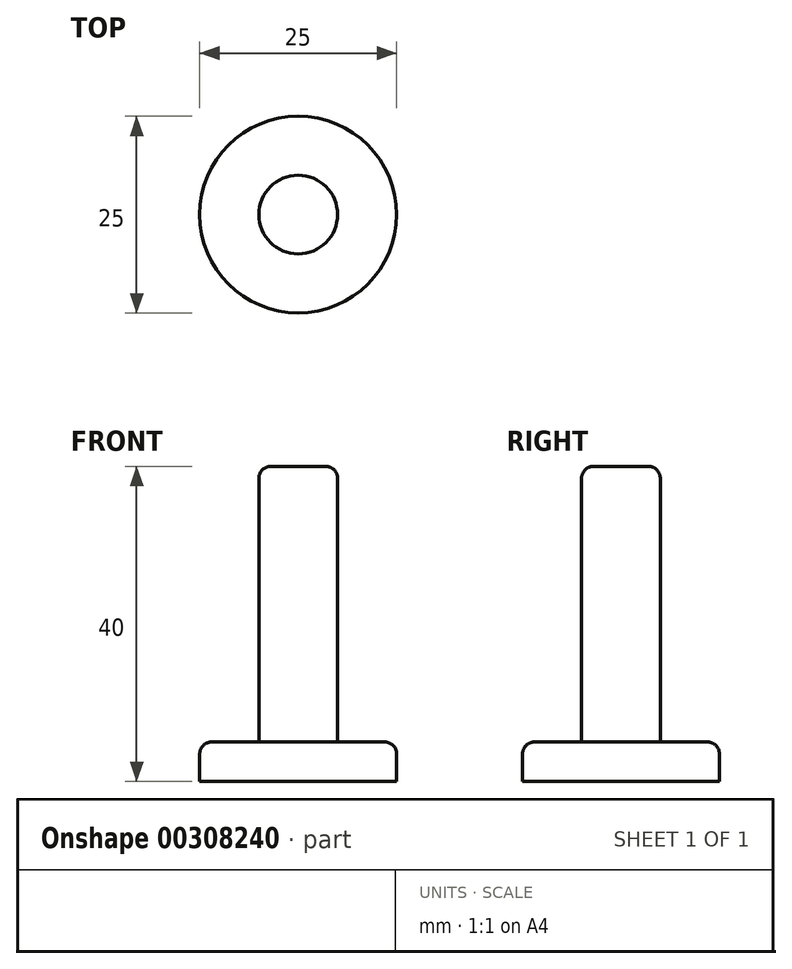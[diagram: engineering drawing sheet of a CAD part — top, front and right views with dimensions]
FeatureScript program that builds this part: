
annotation { "Feature Type Name" : "Feature", "Feature Type Description" : "" }
export const myFeature = defineFeature(function(context is Context, id is Id, definition is map)
    precondition{}
    {
        {
            var Q0;
            Q0=qCreatedBy(makeId("Top.planeOp"),FACE);
            var sketch = newSketch(context, id + "F0", { "sketchPlane" : qUnion([Q0])});
            skCircle(sketch, "E0", {"center": v(0, 0) * mm, "radius": 12.5 * mm});
            skSolve(sketch);
        }
        {
            var Q0;
            Q0=makeQuery(id+"F0.imprint","IMPRINT",FACE,{"disambiguationData":[TD([[makeQuery(id+"F0.imprint","IMPRINT",EDGE,{"derivedFrom":sQuery(id+"F0.wireOp",EDGE,"E0")}),1.0]])]});
            extrude(context, id + "F1", {"entities" : qUnion([Q0]), "depth" : 5 * mm, "offsetDistance" : 25 * mm});
        }
        {
            var Q0;
            Q0=makeQuery(id+"F1.opExtrude","CAP_FACE",FACE,{"disambiguationData":[OSD([sQuery(id+"F0.wireOp",EDGE,"E0")])],"isStart":false});
            var sketch = newSketch(context, id + "F2", { "sketchPlane" : qUnion([Q0])});
            skCircle(sketch, "E1", {"center": v(0, 0) * mm, "radius": 5 * mm});
            skSolve(sketch);
        }
        {
            var Q0;
            Q0=makeQuery(id+"F2.imprint","IMPRINT",FACE,{"disambiguationData":[TD([[makeQuery(id+"F2.imprint","IMPRINT",EDGE,{"derivedFrom":sQuery(id+"F2.wireOp",EDGE,"E1")}),1.0]])]});
            extrude(context, id + "F3", {"entities" : qUnion([Q0]), "depth" : 35 * mm, "offsetDistance" : 25 * mm});
        }
        {
            var Q0;
            Q0=makeQuery(id+"F3.opExtrude","CAP_EDGE",EDGE,{"disambiguationData":[OSD([sQuery(id+"F2.wireOp",EDGE,"E1")])],"isStart":false});
            var Q1;
            Q1=makeQuery(id+"F1.opExtrude","CAP_EDGE",EDGE,{"disambiguationData":[OSD([sQuery(id+"F0.wireOp",EDGE,"E0")])],"isStart":false});
            fillet(context, id + "F4", {"entities" : qUnion([Q0, Q1]), "tangentPropagation" : true, "radius" : 1.5 * mm, "defaultsChanged" : true, "vertexSettings" : [], "allowEdgeOverflow" : false});
        }
    });
